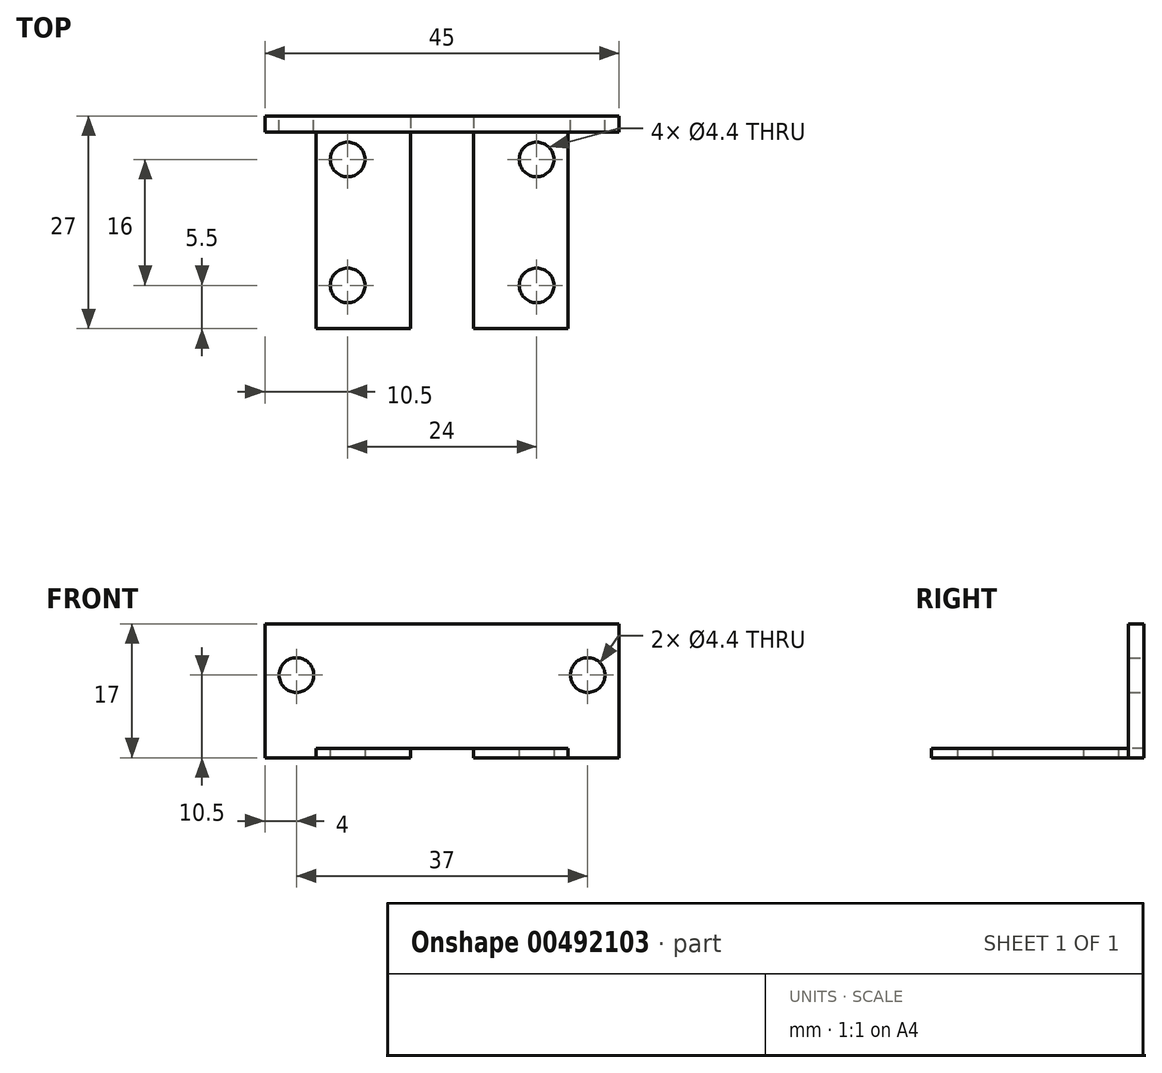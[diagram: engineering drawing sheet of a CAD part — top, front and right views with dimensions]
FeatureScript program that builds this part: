
annotation { "Feature Type Name" : "Feature", "Feature Type Description" : "" }
export const myFeature = defineFeature(function(context is Context, id is Id, definition is map)
    precondition{}
    {
        {
            var Q0;
            Q0=qCreatedBy(makeId("Top.planeOp"),FACE);
            var sketch = newSketch(context, id + "F0", { "sketchPlane" : qUnion([Q0])});
            skLineSegment(sketch, "E0.bottom", {"start": v(-22.5, 13.5) * mm, "end": v(22.5, 13.5) * mm});
            skLineSegment(sketch, "E0.top", {"start": v(-22.5, -13.5) * mm, "end": v(22.5, -13.5) * mm});
            skLineSegment(sketch, "E0.left", {"start": v(-22.5, 13.5) * mm, "end": v(-22.5, -13.5) * mm});
            skLineSegment(sketch, "E0.right", {"start": v(22.5, 13.5) * mm, "end": v(22.5, -13.5) * mm});
            skSolve(sketch);
        }
        {
            var Q0;
            Q0 = qSketchRegion(id + "F0", true);
            extrude(context, id + "F1", {"entities" : qUnion([Q0]), "depth" : (16 + 1) * mm});
        }
        {
            var Q0;
            Q0=makeQuery(id+"F1.opExtrude","SWEPT_FACE",FACE,{"disambiguationData":[OSD([sQuery(id+"F0.wireOp",EDGE,"E0.right")])]});
            var sketch = newSketch(context, id + "F2", { "sketchPlane" : qUnion([Q0])});
            skLineSegment(sketch, "E1.bottom", {"start": v(-13.5, 17) * mm, "end": v(11.5, 17) * mm});
            skLineSegment(sketch, "E1.top", {"start": v(-13.5, 1.2) * mm, "end": v(11.5, 1.2) * mm});
            skLineSegment(sketch, "E1.left", {"start": v(-13.5, 17) * mm, "end": v(-13.5, 1.2) * mm});
            skLineSegment(sketch, "E1.right", {"start": v(11.5, 17) * mm, "end": v(11.5, 1.2) * mm});
            skSolve(sketch);
        }
        {
            var Q0;
            Q0 = qSketchRegion(id + "F2", true);
            extrude(context, id + "F3", {"entities" : qUnion([Q0]), "operationType" : NewBodyOperationType.REMOVE, "endBound" : BoundingType.THROUGH_ALL, "oppositeDirection" : true, "depth" : 25 * mm});
        }
        {
            var Q0;
            Q0=makeQuery(id+"F3.boolean.opBoolean","COPY",FACE,{"derivedFrom":makeQuery(id+"F3.opExtrude","SWEPT_FACE",FACE,{"disambiguationData":[OSD([sQuery(id+"F2.wireOp",EDGE,"E1.top")])]})});
            var sketch = newSketch(context, id + "F4", { "sketchPlane" : qUnion([Q0])});
            skLineSegment(sketch, "E2.bottom", {"start": v(4, 13.5) * mm, "end": v(-4, 13.5) * mm});
            skLineSegment(sketch, "E2.top", {"start": v(4, -13.5) * mm, "end": v(-4, -13.5) * mm});
            skLineSegment(sketch, "E2.left", {"start": v(4, 13.5) * mm, "end": v(4, -13.5) * mm});
            skLineSegment(sketch, "E2.right", {"start": v(-4, 13.5) * mm, "end": v(-4, -13.5) * mm});
            skSolve(sketch);
        }
        {
            var Q0;
            Q0 = qSketchRegion(id + "F4", true);
            extrude(context, id + "F5", {"entities" : qUnion([Q0]), "operationType" : NewBodyOperationType.REMOVE, "endBound" : BoundingType.THROUGH_ALL, "oppositeDirection" : true, "depth" : 1 * mm});
        }
        {
            var Q0;
            Q0=makeQuery(id+"F0.imprint","IMPRINT",FACE,{"disambiguationData":[TD([[makeQuery(id+"F0.imprint","IMPRINT",EDGE,{"derivedFrom":sQuery(id+"F0.wireOp",EDGE,"E0.bottom")}),-1.0]])]});
            var sketch = newSketch(context, id + "F6", { "sketchPlane" : qUnion([Q0])});
            skPoint(sketch, "E3", {"position": v(12, -8) * mm});
            skPoint(sketch, "E4", {"position": v(-12, -8) * mm});
            skPoint(sketch, "E5", {"position": v(-12, 8) * mm});
            skPoint(sketch, "E6", {"position": v(12, 8) * mm});
            skSolve(sketch);
        }
        {
            var Q0;
            Q0=sQuery(id+"F6.wireOp",VERTEX,"E4");
            var Q1;
            Q1=sQuery(id+"F6.wireOp",VERTEX,"E3");
            var Q2;
            Q2=sQuery(id+"F6.wireOp",VERTEX,"E6");
            var Q3;
            Q3=sQuery(id+"F6.wireOp",VERTEX,"E5");
            var Q4;
            Q4=makeQuery(id+"F1.opExtrude","SWEPT_BODY",BODY,{"disambiguationData":[OSD([sQuery(id+"F0.wireOp",EDGE,"E0.bottom"),sQuery(id+"F0.wireOp",EDGE,"E0.top"),sQuery(id+"F0.wireOp",EDGE,"E0.left"),sQuery(id+"F0.wireOp",EDGE,"E0.right")])]});
            hole(context, id + "F7", {"style" : HoleStyle.SIMPLE, "endStyle" : HoleEndStyle.THROUGH, "oppositeDirection" : true, "standardTappedOrClearance" : lookupTablePath({ "standard" : "ISO", "fit" : "Normal", "size" : "M4", "type" : "Clearance" }), "standardBlindInLast" : lookupTablePath({ "fit" : "Standard", "standard" : "ISO", "size" : "M4", "type" : "Clearance" }), "holeDiameter" : 4.4 * mm, "isTappedThrough" : true, "tappedDepth" : 12 * mm, "tapClearance" : 3, "locations" : qUnion([Q0, Q1, Q2, Q3]), "scope" : qUnion([Q4])});
        }
        {
            var Q0;
            Q0=makeQuery(id+"F1.opExtrude","SWEPT_FACE",FACE,{"disambiguationData":[OSD([sQuery(id+"F0.wireOp",EDGE,"E0.bottom")])]});
            var sketch = newSketch(context, id + "F8", { "sketchPlane" : qUnion([Q0])});
            skPoint(sketch, "E7", {"position": v(18.5, 10.5) * mm});
            skPoint(sketch, "E8", {"position": v(-18.5, 10.5) * mm});
            skSolve(sketch);
        }
        {
            var Q0;
            Q0=sQuery(id+"F8.wireOp",VERTEX,"E7");
            var Q1;
            Q1=sQuery(id+"F8.wireOp",VERTEX,"E8");
            var Q2;
            Q2=makeQuery(id+"F1.opExtrude","SWEPT_BODY",BODY,{"disambiguationData":[OSD([sQuery(id+"F0.wireOp",EDGE,"E0.bottom"),sQuery(id+"F0.wireOp",EDGE,"E0.top"),sQuery(id+"F0.wireOp",EDGE,"E0.left"),sQuery(id+"F0.wireOp",EDGE,"E0.right")])]});
            hole(context, id + "F9", {"style" : HoleStyle.SIMPLE, "endStyle" : HoleEndStyle.THROUGH, "standardTappedOrClearance" : lookupTablePath({ "standard" : "ISO", "fit" : "Normal", "size" : "M4", "type" : "Clearance" }), "standardBlindInLast" : lookupTablePath({ "fit" : "Standard", "standard" : "ISO", "size" : "M4", "type" : "Clearance" }), "holeDiameter" : 4.4 * mm, "isTappedThrough" : true, "tappedDepth" : 12 * mm, "tapClearance" : 3, "locations" : qUnion([Q0, Q1]), "scope" : qUnion([Q2])});
        }
        {
            var Q0;
            {var subQ1=sQuery(id+"F2.wireOp",EDGE,"E1.top");var subQ6=makeQuery(id+"F3.boolean.opBoolean","INTERSECT",EDGE,{"derivedFrom":[makeQuery(id+"F1.opExtrude","SWEPT_FACE",FACE,{"disambiguationData":[OSD([sQuery(id+"F0.wireOp",EDGE,"E0.left")])]}),makeQuery(id+"F3.opExtrude","SWEPT_FACE",FACE,{"disambiguationData":[OSD([subQ1])]})]});Q0=makeQuery(id+"F4.imprint","IMPRINT",FACE,{"disambiguationData":[TD([[makeQuery(id+"F4.imprint","IMPRINT",EDGE,{"derivedFrom":subQ6}),-1.0]])]});}
            var sketch = newSketch(context, id + "F10", { "sketchPlane" : qUnion([Q0])});
            skLineSegment(sketch, "E9.bottom", {"start": v(-22.5, -13.5) * mm, "end": v(-16, -13.5) * mm});
            skLineSegment(sketch, "E9.top", {"start": v(-22.5, 11.5) * mm, "end": v(-16, 11.5) * mm});
            skLineSegment(sketch, "E9.left", {"start": v(-22.5, -13.5) * mm, "end": v(-22.5, 11.5) * mm});
            skLineSegment(sketch, "E9.right", {"start": v(-16, -13.5) * mm, "end": v(-16, 11.5) * mm});
            skLineSegment(sketch, "E10.bottom", {"start": v(22.5, -13.5) * mm, "end": v(16, -13.5) * mm});
            skLineSegment(sketch, "E10.top", {"start": v(22.5, 11.5) * mm, "end": v(16, 11.5) * mm});
            skLineSegment(sketch, "E10.left", {"start": v(22.5, -13.5) * mm, "end": v(22.5, 11.5) * mm});
            skLineSegment(sketch, "E10.right", {"start": v(16, -13.5) * mm, "end": v(16, 11.5) * mm});
            skSolve(sketch);
        }
        {
            var Q0;
            Q0 = qSketchRegion(id + "F10", true);
            extrude(context, id + "F11", {"entities" : qUnion([Q0]), "operationType" : NewBodyOperationType.REMOVE, "endBound" : BoundingType.THROUGH_ALL, "oppositeDirection" : true, "depth" : 25 * mm});
        }
    });
